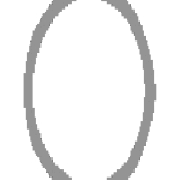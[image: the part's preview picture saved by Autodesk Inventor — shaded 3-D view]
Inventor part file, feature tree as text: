
AUTODESK INVENTOR PART (.ipt)
format: ipt  version: 2021 (Build 250183000, 183)  size: 110,080 bytes
history: native  units: in
note: dims shown in document units (in); Inventor stores cm internally (conversion verified against a paired STEP export)
features: other x4, sketch x3, plane x1
ambient origin geometry x8: Origin, YZ Plane, XZ Plane, XY Plane, X Axis, Y Axis, Z Axis, Center Point
bodies: Solid1 (feature_tree), Body (feature_tree)
feature tree (8):
  other  "Driven Length"
  other  "Frame Generator"
  other  "Start Plane"
  other  "End Plane"
  sketch  "Sketch"  dims[d2=20.0811in d4=-0.0in d5=20.0811in d6=0.12in d7=0.0in d8=90.0deg d9=20.0811in]
  sketch  "Sketch2"  dims[d0=1.0in]
  plane  "Work Plane3"
  sketch  "Sketch3"  dims[d1=0.065in]
